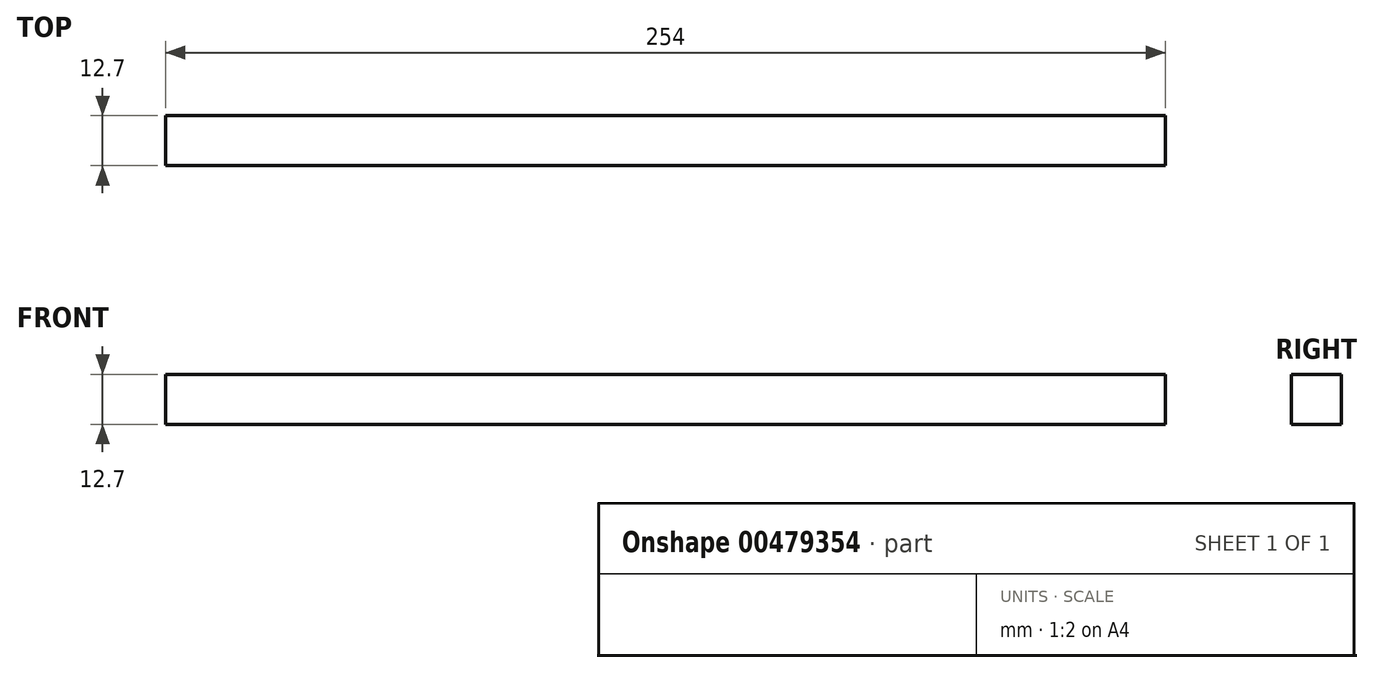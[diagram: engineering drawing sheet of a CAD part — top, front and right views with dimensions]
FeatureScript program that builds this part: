
annotation { "Feature Type Name" : "Feature", "Feature Type Description" : "" }
export const myFeature = defineFeature(function(context is Context, id is Id, definition is map)
    precondition{}
    {
        {
            var Q0;
            Q0=qCreatedBy(makeId("Front.planeOp"),FACE);
            var sketch = newSketch(context, id + "F0", { "sketchPlane" : qUnion([Q0])});
            skLineSegment(sketch, "E0.bottom", {"start": v(0, 0) * mm, "end": v(254, 0) * mm});
            skLineSegment(sketch, "E0.top", {"start": v(0, 12.7) * mm, "end": v(254, 12.7) * mm});
            skLineSegment(sketch, "E0.left", {"start": v(0, 0) * mm, "end": v(0, 12.7) * mm});
            skLineSegment(sketch, "E0.right", {"start": v(254, 0) * mm, "end": v(254, 12.7) * mm});
            skSolve(sketch);
        }
        {
            var Q0;
            Q0 = qSketchRegion(id + "F0", true);
            extrude(context, id + "F1", {"entities" : qUnion([Q0]), "depth" : 12.7 * mm});
        }
    });
